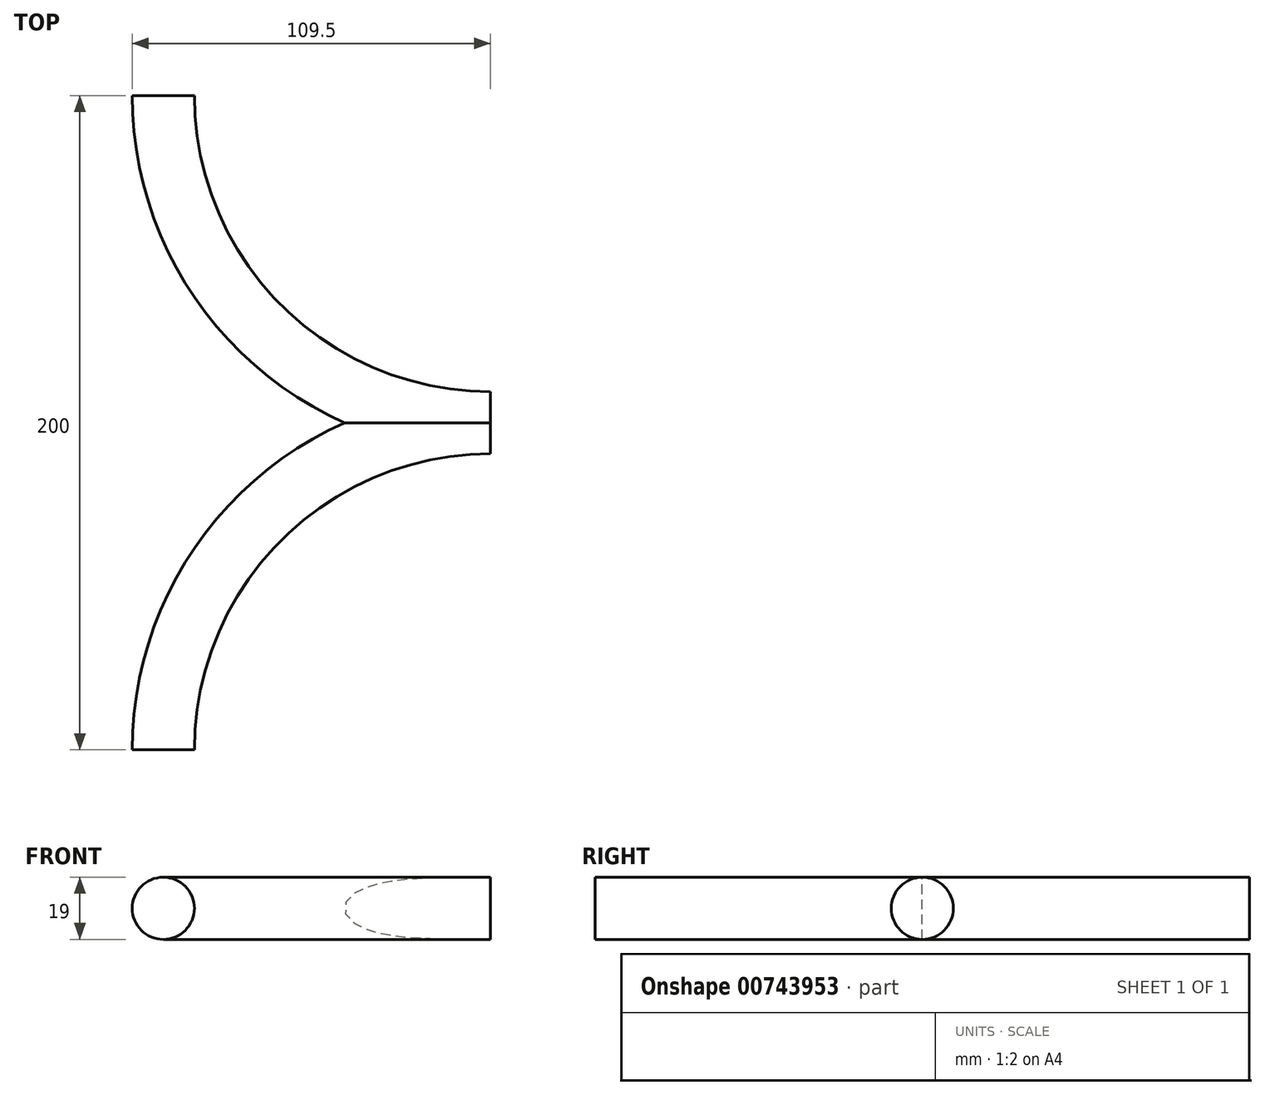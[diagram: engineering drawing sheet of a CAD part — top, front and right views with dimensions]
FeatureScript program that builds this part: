
annotation { "Feature Type Name" : "Feature", "Feature Type Description" : "" }
export const myFeature = defineFeature(function(context is Context, id is Id, definition is map)
    precondition{}
    {
        {
            var Q0;
            Q0=qCreatedBy(makeId("Top.planeOp"),FACE);
            var sketch = newSketch(context, id + "F0", { "sketchPlane" : qUnion([Q0])});
            skLineSegment(sketch, "E0", {"start": v(0, 0) * mm, "end": v(100, 0) * mm});
            skLineSegment(sketch, "E1", {"start": v(0, 0) * mm, "end": v(0, 100) * mm});
            skArc(sketch, "E2", {"start": v(0, 100) * mm, "mid": v(29.29, 29.29) * mm, "end": v(100, 0) * mm});
            skSolve(sketch);
        }
        {
            var Q0;
            Q0=qCreatedBy(makeId("Right.planeOp"),FACE);
            cPlane(context, id + "F1", {"entities" : qUnion([Q0]), "cplaneType" : CPlaneType.OFFSET, "offset" : 100 * mm, "width" : 150 * mm, "height" : 150 * mm});
        }
        {
            var Q0;
            Q0=qCreatedBy(id+"F1.planeOp",FACE);
            var sketch = newSketch(context, id + "F2", { "sketchPlane" : qUnion([Q0])});
            skCircle(sketch, "E3", {"center": v(0, 0) * mm, "radius": 9.5 * mm});
            skSolve(sketch);
        }
        {
            var Q0;
            Q0=makeQuery(id+"F2.imprint","IMPRINT",FACE,{"disambiguationData":[TD([[makeQuery(id+"F2.imprint","IMPRINT",EDGE,{"derivedFrom":sQuery(id+"F2.wireOp",EDGE,"E3")}),1.0]])]});
            var Q1;
            Q1=sQuery(id+"F0.wireOp",EDGE,"E2");
            sweep(context, id + "F3", {"profiles" : qUnion([Q0]), "path" : qUnion([Q1])});
        }
        {
            var Q0;
            Q0=qCreatedBy(makeId("Front.planeOp"),FACE);
            var sketch = newSketch(context, id + "F4", { "sketchPlane" : qUnion([Q0])});
            skLineSegment(sketch, "E4.bottom", {"start": v(-111, 147.18) * mm, "end": v(156.03, 147.18) * mm});
            skLineSegment(sketch, "E4.top", {"start": v(-111, -145.65) * mm, "end": v(156.03, -145.65) * mm});
            skLineSegment(sketch, "E4.left", {"start": v(-111, 147.18) * mm, "end": v(-111, -145.65) * mm});
            skLineSegment(sketch, "E4.right", {"start": v(156.03, 147.18) * mm, "end": v(156.03, -145.65) * mm});
            skSolve(sketch);
        }
        {
            var Q0;
            Q0 = qSketchRegion(id + "F4", true);
            extrude(context, id + "F5", {"entities" : qUnion([Q0]), "operationType" : NewBodyOperationType.REMOVE, "depth" : 40.8 * mm, "offsetDistance" : 25 * mm});
        }
        {
            var Q0;
            Q0=makeQuery(id+"F3.opSweep","SWEPT_BODY",BODY,{"disambiguationData":[OSD([sQuery(id+"F0.wireOp",EDGE,"E2"),sQuery(id+"F2.wireOp",EDGE,"E3")])]});
            var Q1;
            Q1=makeQuery(id+"F5.boolean.opBoolean","COPY",FACE,{"derivedFrom":makeQuery(id+"F5.opExtrude","CAP_FACE",FACE,{"disambiguationData":[OSD([sQuery(id+"F4.wireOp",EDGE,"E4.bottom"),sQuery(id+"F4.wireOp",EDGE,"E4.top"),sQuery(id+"F4.wireOp",EDGE,"E4.left"),sQuery(id+"F4.wireOp",EDGE,"E4.right")])],"isStart":true})});
            mirror(context, id + "F6", {"operationType" : NewBodyOperationType.ADD, "entities" : qUnion([Q0]), "mirrorPlane" : qUnion([Q1])});
        }
    });
